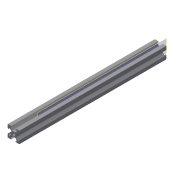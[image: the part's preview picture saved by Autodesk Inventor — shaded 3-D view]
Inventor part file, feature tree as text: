
AUTODESK INVENTOR PART (.ipt)
format: ipt  version: 2019.4 (Build 234330000, 330)  size: 153,600 bytes
history: native  units: mm
features: other x2, extrude x1, plane x1, sketch x1, reference x1
ambient origin geometry x8: Origin, YZ Plane, XZ Plane, XY Plane, X Axis, Y Axis, Z Axis, Center Point
bodies: Solid1 (feature_tree)
feature tree (6):
  extrude  "Extrusion1"  [1 undecoded]
  plane  "Work Plane1"
  sketch  "Sketch1"  dims[d0=250.0mm d1=0.0mm]
  reference  "Reference1"
  other  "Assembly_neje_slide_y_wellplateholder_20mmrod.iam"
  other  "00_V-Slot_20x:1"
note: 1 required parameter value undecoded (feature->parameter linkage not recoverable at this tier; creation-order binding heuristic only, values carry confidence <= 0.55)
